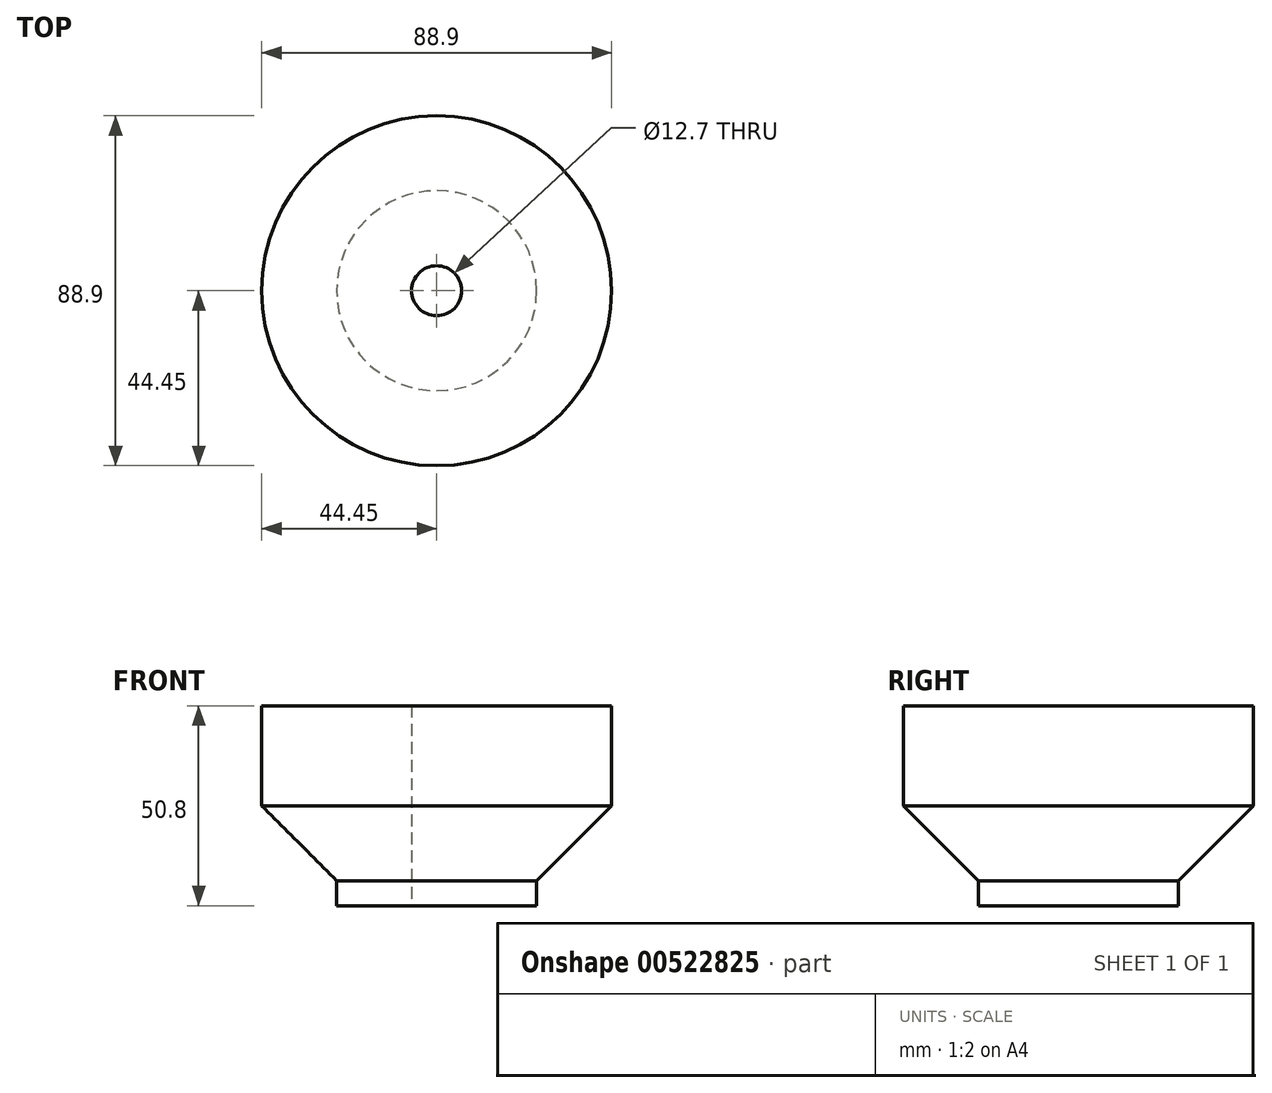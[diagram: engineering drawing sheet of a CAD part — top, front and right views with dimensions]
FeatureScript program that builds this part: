
annotation { "Feature Type Name" : "Feature", "Feature Type Description" : "" }
export const myFeature = defineFeature(function(context is Context, id is Id, definition is map)
    precondition{}
    {
        {
            var Q0;
            Q0=qCreatedBy(makeId("Front.planeOp"),FACE);
            var sketch = newSketch(context, id + "F0", { "sketchPlane" : qUnion([Q0])});
            skLineSegment(sketch, "E0", {"start": v(6.35, 0) * mm, "end": v(25.4, 0) * mm});
            skLineSegment(sketch, "E1", {"start": v(25.4, 0) * mm, "end": v(25.4, 6.35) * mm});
            skLineSegment(sketch, "E2", {"start": v(25.4, 6.35) * mm, "end": v(44.45, 25.4) * mm});
            skLineSegment(sketch, "E3", {"start": v(44.45, 25.4) * mm, "end": v(44.45, 50.8) * mm});
            skLineSegment(sketch, "E4", {"start": v(44.45, 50.8) * mm, "end": v(6.35, 50.8) * mm});
            skLineSegment(sketch, "E5", {"start": v(6.35, 50.8) * mm, "end": v(6.35, 0) * mm});
            skLineSegment(sketch, "E6", {"start": v(0, 0) * mm, "end": v(0, 69.95) * mm, "construction": true});
            skSolve(sketch);
        }
        {
            var Q0;
            Q0=makeQuery(id+"F0.imprint","IMPRINT",FACE,{"disambiguationData":[TD([[makeQuery(id+"F0.imprint","IMPRINT",EDGE,{"derivedFrom":sQuery(id+"F0.wireOp",EDGE,"E0")}),1.0]])]});
            var Q1;
            Q1=sQuery(id+"F0.wireOp",EDGE,"E6");
            revolve(context, id + "F1", {"entities" : qUnion([Q0]), "axis" : qUnion([Q1]), "revolveType" : RevolveType.FULL});
        }
    });
